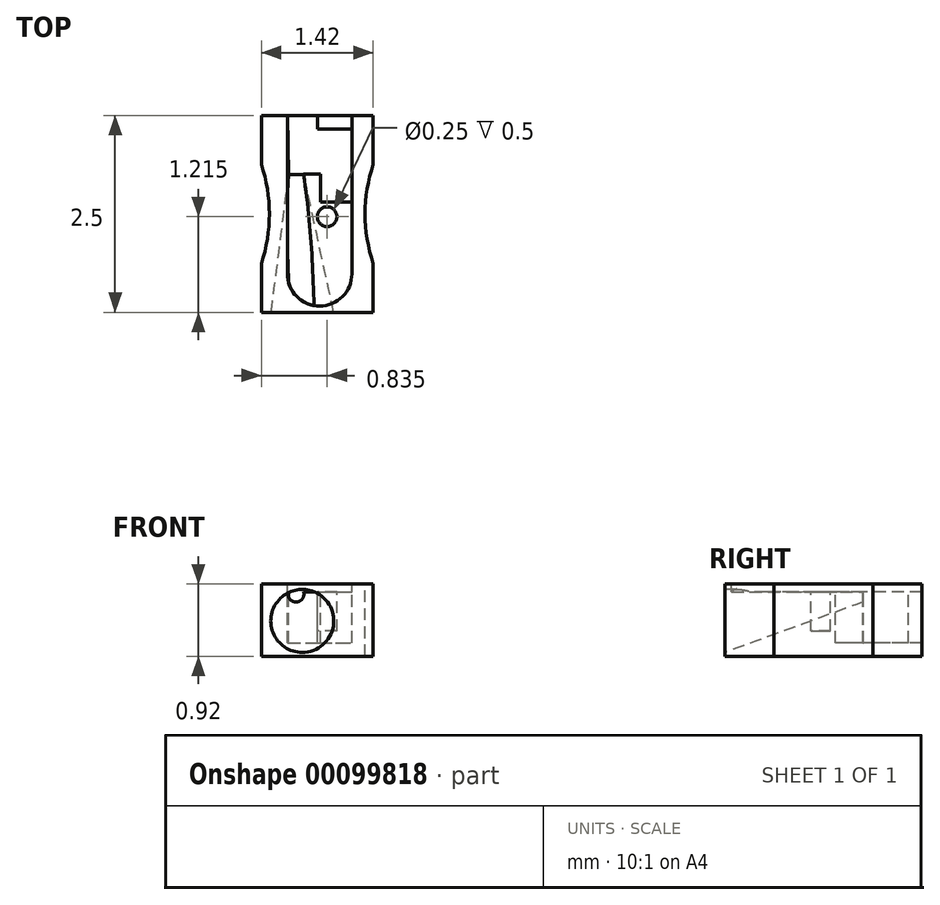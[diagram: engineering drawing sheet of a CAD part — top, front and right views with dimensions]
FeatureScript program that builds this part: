
annotation { "Feature Type Name" : "Feature", "Feature Type Description" : "" }
export const myFeature = defineFeature(function(context is Context, id is Id, definition is map)
    precondition{}
    {
        {
            var Q0;
            Q0=qCreatedBy(makeId("Front.planeOp"),FACE);
            var sketch = newSketch(context, id + "F0", { "sketchPlane" : qUnion([Q0])});
            skLineSegment(sketch, "E0", {"start": v(0.71, 0) * mm, "end": v(0.71, 0.92) * mm});
            skLineSegment(sketch, "E1", {"start": v(0.71, 0.92) * mm, "end": v(0, 0.92) * mm});
            skLineSegment(sketch, "E2", {"start": v(0, 0) * mm, "end": v(0.71, 0) * mm});
            skLineSegment(sketch, "E3.MirrorCS", {"start": v(-0.71, 0.92) * mm, "end": v(0, 0.92) * mm});
            skLineSegment(sketch, "E4.MirrorCS", {"start": v(-0.71, 0) * mm, "end": v(-0.71, 0.92) * mm});
            skLineSegment(sketch, "E5.MirrorCS", {"start": v(0, 0) * mm, "end": v(-0.71, 0) * mm});
            skSolve(sketch);
        }
        {
            var Q0;
            Q0 = qSketchRegion(id + "F0", true);
            extrude(context, id + "F1", {"entities" : qUnion([Q0]), "depth" : 2.5 * mm});
        }
        {
            var Q0;
            Q0=makeQuery(id+"F1.opExtrude","SWEPT_FACE",FACE,{"disambiguationData":[OSD([sQuery(id+"F0.wireOp",EDGE,"E1"),sQuery(id+"F0.wireOp",EDGE,"E3.MirrorCS")])]});
            var sketch = newSketch(context, id + "F2", { "sketchPlane" : qUnion([Q0])});
            skLineSegment(sketch, "E6", {"start": v(-0.38, 0) * mm, "end": v(-0.38, -2) * mm});
            skLineSegment(sketch, "E7", {"start": v(0.44, 0) * mm, "end": v(0.44, -2) * mm});
            skArc(sketch, "E8", {"start": v(-0.38, -2) * mm, "mid": v(0.03, -2.42) * mm, "end": v(0.44, -2) * mm});
            skLineSegment(sketch, "E9", {"start": v(-0.38, 0) * mm, "end": v(0.44, 0) * mm});
            skSolve(sketch);
        }
        {
            var Q0;
            Q0 = qSketchRegion(id + "F2", true);
            extrude(context, id + "F3", {"entities" : qUnion([Q0]), "operationType" : NewBodyOperationType.REMOVE, "oppositeDirection" : true, "depth" : 0.1 * mm});
        }
        {
            var Q0;
            Q0=makeQuery(id+"F1.opExtrude","CAP_FACE",FACE,{"disambiguationData":[OSD([sQuery(id+"F0.wireOp",EDGE,"E0"),sQuery(id+"F0.wireOp",EDGE,"E1"),sQuery(id+"F0.wireOp",EDGE,"E2"),sQuery(id+"F0.wireOp",EDGE,"E3.MirrorCS"),sQuery(id+"F0.wireOp",EDGE,"E4.MirrorCS"),sQuery(id+"F0.wireOp",EDGE,"E5.MirrorCS")])],"isStart":false});
            var sketch = newSketch(context, id + "F4", { "sketchPlane" : qUnion([Q0])});
            skCircle(sketch, "E10", {"center": v(-0.2, 0.45) * mm, "radius": 0.4 * mm});
            skSolve(sketch);
        }
        {
            var Q0;
            Q0=makeQuery(id+"F4.imprint","IMPRINT",FACE,{"disambiguationData":[TD([[makeQuery(id+"F4.imprint","IMPRINT",EDGE,{"derivedFrom":sQuery(id+"F4.wireOp",EDGE,"E10")}),-1.0]])]});
            cPlane(context, id + "F5", {"entities" : qUnion([Q0]), "cplaneType" : CPlaneType.OFFSET, "offset" : 1.75 * mm, "oppositeDirection" : true, "width" : 150 * mm, "height" : 150 * mm});
        }
        {
            var Q0;
            Q0=qCreatedBy(id+"F5.planeOp",FACE);
            var sketch = newSketch(context, id + "F6", { "sketchPlane" : qUnion([Q0])});
            skCircle(sketch, "E11", {"center": v(-0.27, 0.79) * mm, "radius": 0.1 * mm});
            skSolve(sketch);
        }
        {
            var Q1;
            Q1 = qSketchRegion(id + "F4", true);
            var Q2;
            Q2 = qSketchRegion(id + "F6", true);
            loft(context, id + "F7", {"operationType" : NewBodyOperationType.REMOVE, "sheetProfilesArray" : [{ "sheetProfileEntities" : qUnion([Q1]) }, { "sheetProfileEntities" : qUnion([Q2]) }]});
        }
        {
            var Q0;
            Q0=makeQuery(id+"F3.boolean.opBoolean","COPY",FACE,{"derivedFrom":makeQuery(id+"F3.opExtrude","CAP_FACE",FACE,{"disambiguationData":[OSD([sQuery(id+"F2.wireOp",EDGE,"E6"),sQuery(id+"F2.wireOp",EDGE,"E7"),sQuery(id+"F2.wireOp",EDGE,"E8"),sQuery(id+"F2.wireOp",EDGE,"E9")])],"isStart":false})});
            var sketch = newSketch(context, id + "F8", { "sketchPlane" : qUnion([Q0])});
            skSolve(sketch);
        }
        {
            var Q0;
            Q0=makeQuery(id+"F3.boolean.opBoolean","COPY",FACE,{"derivedFrom":makeQuery(id+"F3.opExtrude","CAP_FACE",FACE,{"disambiguationData":[OSD([sQuery(id+"F2.wireOp",EDGE,"E6"),sQuery(id+"F2.wireOp",EDGE,"E7"),sQuery(id+"F2.wireOp",EDGE,"E8"),sQuery(id+"F2.wireOp",EDGE,"E9")])],"isStart":false})});
            var sketch = newSketch(context, id + "F9", { "sketchPlane" : qUnion([Q0])});
            skLineSegment(sketch, "E12", {"start": v(-0.38, 0) * mm, "end": v(-0.37, -0.75) * mm});
            skLineSegment(sketch, "E13", {"start": v(-0.38, 0) * mm, "end": v(0, 0) * mm});
            skLineSegment(sketch, "E14", {"start": v(0, 0) * mm, "end": v(0, -0.17) * mm});
            skLineSegment(sketch, "E15", {"start": v(0, -0.17) * mm, "end": v(0.44, -0.17) * mm});
            skLineSegment(sketch, "E16", {"start": v(0.44, -0.17) * mm, "end": v(0.44, -1.1) * mm});
            skLineSegment(sketch, "E17", {"start": v(0.04, -1.1) * mm, "end": v(0.44, -1.1) * mm});
            skLineSegment(sketch, "E18", {"start": v(-0.37, -0.75) * mm, "end": v(0.04, -0.74) * mm});
            skLineSegment(sketch, "E19", {"start": v(0.04, -0.74) * mm, "end": v(0.04, -1.1) * mm});
            skSolve(sketch);
        }
        {
            var Q0;
            Q0 = qSketchRegion(id + "F9", true);
            extrude(context, id + "F10", {"entities" : qUnion([Q0]), "operationType" : NewBodyOperationType.REMOVE, "oppositeDirection" : true, "depth" : 0.65 * mm});
        }
        {
            var Q0;
            Q0=makeQuery(id+"F1.opExtrude","SWEPT_FACE",FACE,{"disambiguationData":[OSD([sQuery(id+"F0.wireOp",EDGE,"E1"),sQuery(id+"F0.wireOp",EDGE,"E3.MirrorCS")])]});
            var sketch = newSketch(context, id + "F11", { "sketchPlane" : qUnion([Q0])});
            skLineSegment(sketch, "E20", {"start": v(0.71, 0) * mm, "end": v(0.71, -0.62) * mm});
            skLineSegment(sketch, "E21", {"start": v(0.71, -2.5) * mm, "end": v(0.71, -1.88) * mm});
            skArc(sketch, "E22", {"start": v(0.7, -0.62) * mm, "mid": v(0.6, -1.25) * mm, "end": v(0.71, -1.88) * mm});
            skLineSegment(sketch, "E23", {"start": v(0.71, -0.62) * mm, "end": v(0.71, -1.88) * mm});
            skArc(sketch, "E24.MirrorCS", {"start": v(-0.7, -0.62) * mm, "mid": v(-0.6, -1.25) * mm, "end": v(-0.71, -1.88) * mm});
            skLineSegment(sketch, "E25.MirrorCS", {"start": v(-0.71, -0.62) * mm, "end": v(-0.71, -1.88) * mm});
            skLineSegment(sketch, "E26.MirrorCS", {"start": v(-0.71, 0) * mm, "end": v(-0.7, -0.62) * mm});
            skLineSegment(sketch, "E27.MirrorCS", {"start": v(-0.71, -2.5) * mm, "end": v(-0.71, -1.88) * mm});
            skSolve(sketch);
        }
        {
            var Q0;
            Q0 = qSketchRegion(id + "F11", true);
            extrude(context, id + "F12", {"entities" : qUnion([Q0]), "operationType" : NewBodyOperationType.REMOVE, "oppositeDirection" : true, "depth" : 25 * mm});
        }
        {
            var Q0;
            {var subQ4=sQuery(id+"F2.wireOp",EDGE,"E6");Q0=makeQuery(id+"F8.imprint","IMPRINT",FACE,{"disambiguationData":[TD([[makeQuery(id+"F8.imprint","IMPRINT",EDGE,{"derivedFrom":makeQuery(id+"F3.boolean.opBoolean","COPY",EDGE,{"derivedFrom":makeQuery(id+"F3.opExtrude","CAP_EDGE",EDGE,{"disambiguationData":[OSD([subQ4])],"isStart":false})})}),1.0]])]});}
            var sketch = newSketch(context, id + "F13", { "sketchPlane" : qUnion([Q0])});
            skSolve(sketch);
        }
        {
            var Q0;
            {var subQ4=sQuery(id+"F2.wireOp",EDGE,"E6");Q0=makeQuery(id+"F8.imprint","IMPRINT",FACE,{"disambiguationData":[TD([[makeQuery(id+"F8.imprint","IMPRINT",EDGE,{"derivedFrom":makeQuery(id+"F3.boolean.opBoolean","COPY",EDGE,{"derivedFrom":makeQuery(id+"F3.opExtrude","CAP_EDGE",EDGE,{"disambiguationData":[OSD([subQ4])],"isStart":false})})}),1.0]])]});}
            var sketch = newSketch(context, id + "F14", { "sketchPlane" : qUnion([Q0])});
            skCircle(sketch, "E28", {"center": v(0.13, -1.29) * mm, "radius": 0.12 * mm});
            skSolve(sketch);
        }
        {
            var Q0;
            Q0 = qSketchRegion(id + "F14", true);
            extrude(context, id + "F15", {"entities" : qUnion([Q0]), "operationType" : NewBodyOperationType.REMOVE, "oppositeDirection" : true, "depth" : 0.5 * mm});
        }
    });
